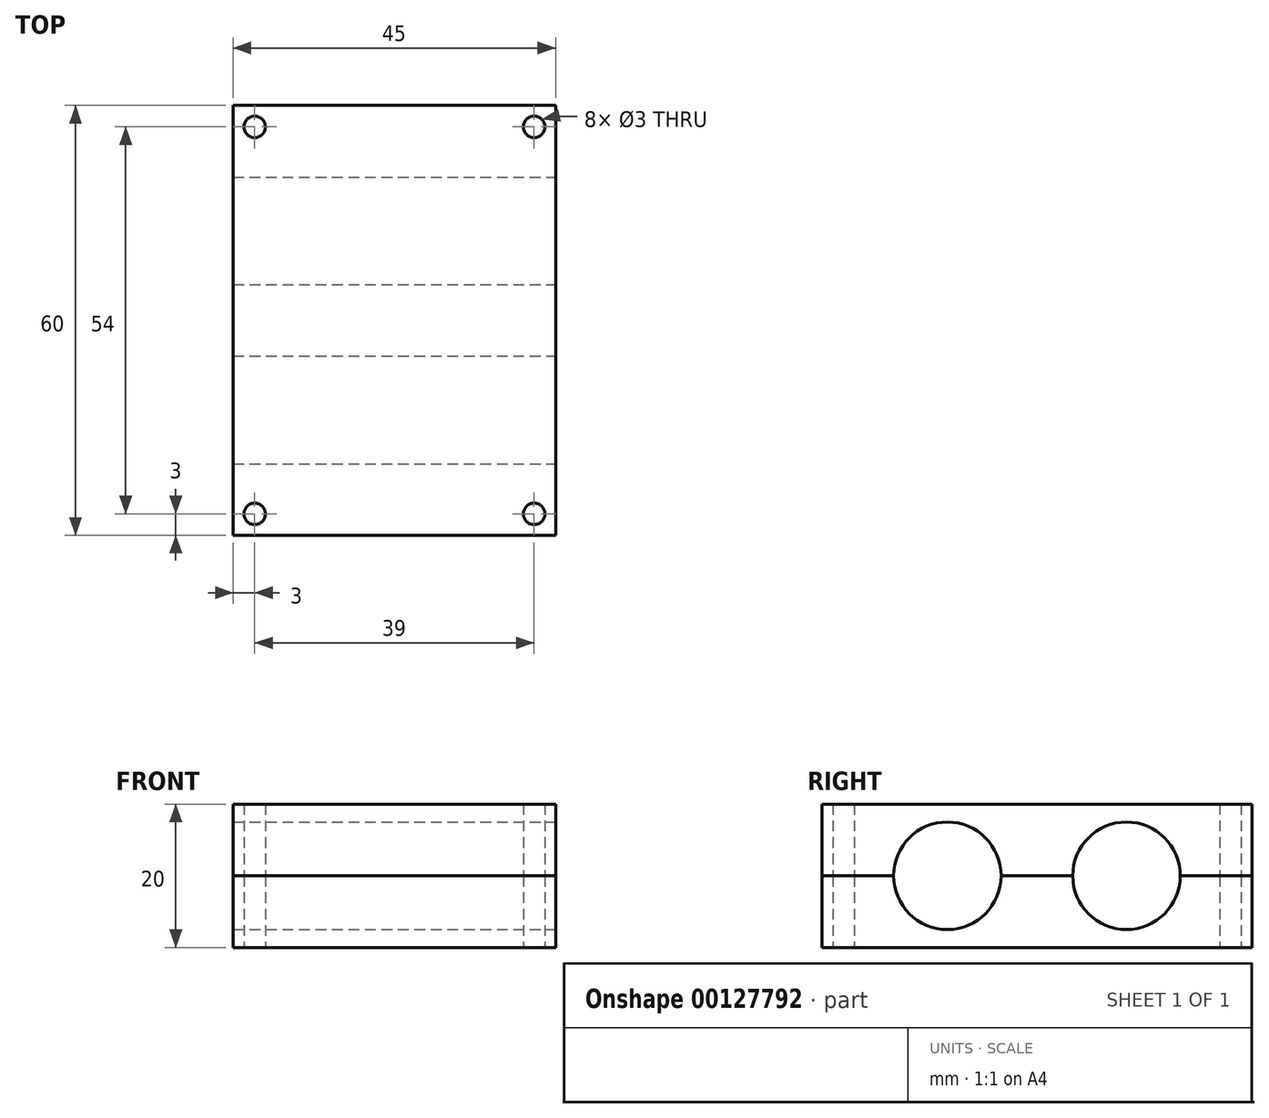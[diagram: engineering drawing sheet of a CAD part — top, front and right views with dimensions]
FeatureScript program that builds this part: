
annotation { "Feature Type Name" : "Feature", "Feature Type Description" : "" }
export const myFeature = defineFeature(function(context is Context, id is Id, definition is map)
    precondition{}
    {
        {
            var Q0;
            Q0=qCreatedBy(makeId("Right.planeOp"),FACE);
            var sketch = newSketch(context, id + "F0", { "sketchPlane" : qUnion([Q0])});
            skLineSegment(sketch, "E0", {"start": v(30, 0) * mm, "end": v(-30, 0) * mm});
            skLineSegment(sketch, "E1", {"start": v(-30, 0) * mm, "end": v(-30, 10) * mm});
            skLineSegment(sketch, "E2", {"start": v(0, 0) * mm, "end": v(0, -33.58) * mm, "construction": true});
            skLineSegment(sketch, "E3.MirrorCS", {"start": v(30, 0) * mm, "end": v(30, 10) * mm});
            skLineSegment(sketch, "E4.MirrorCS", {"start": v(30, 10) * mm, "end": v(-30, 10) * mm});
            skSolve(sketch);
        }
        {
            var Q0;
            Q0 = qSketchRegion(id + "F0", true);
            extrude(context, id + "F1", {"entities" : qUnion([Q0]), "endBound" : BoundingType.SYMMETRIC, "depth" : 45 * mm});
        }
        {
            var Q0;
            Q0=makeQuery(id+"F1.opExtrude","SWEPT_FACE",FACE,{"disambiguationData":[OSD([sQuery(id+"F0.wireOp",EDGE,"E0")])]});
            extrude(context, id + "F2", {"entities" : qUnion([Q0]), "depth" : 10 * mm});
        }
        {
            var Q0;
            Q0=makeQuery(id+"F1.opExtrude","CAP_FACE",FACE,{"disambiguationData":[OSD([sQuery(id+"F0.wireOp",EDGE,"E0"),sQuery(id+"F0.wireOp",EDGE,"E1"),sQuery(id+"F0.wireOp",EDGE,"128Ns7S3-iJ1R-hD63-Des7-Cw0FQeiLVcyu"),sQuery(id+"F0.wireOp",EDGE,"o8RlvnOk-mUnY-sZV7-Nvvh-wG9zo2OJw8qh"),sQuery(id+"F0.wireOp",EDGE,"HRAPB6wn-nVdK-lxr8-JZlT-5lnG8vlRGJTT"),sQuery(id+"F0.wireOp",EDGE,"45f2c6da-1243-415b-b326-b4a96a1e2a690.MirrorCS"),sQuery(id+"F0.wireOp",EDGE,"E3.MirrorCS"),sQuery(id+"F0.wireOp",EDGE,"E4.MirrorCS"),sQuery(id+"F0.wireOp",EDGE,"54c41837-7ab6-4fc5-a0fb-2d965c1fca7a0.MirrorCS"),sQuery(id+"F0.wireOp",EDGE,"8871dbe9-c1a3-435a-abf9-9d9c7d9c37b50.MirrorCS")])],"isStart":false});
            var sketch = newSketch(context, id + "F3", { "sketchPlane" : qUnion([Q0])});
            skCircle(sketch, "E5", {"center": v(-12.5, 0) * mm, "radius": 7.5 * mm});
            skCircle(sketch, "E6", {"center": v(12.5, 0) * mm, "radius": 7.5 * mm});
            skLineSegment(sketch, "E7", {"start": v(0, 0) * mm, "end": v(0, 23.63) * mm, "construction": true});
            skSolve(sketch);
        }
        {
            var Q0;
            Q0 = qSketchRegion(id + "F3", true);
            extrude(context, id + "F4", {"entities" : qUnion([Q0]), "operationType" : NewBodyOperationType.REMOVE, "endBound" : BoundingType.THROUGH_ALL, "oppositeDirection" : true, "depth" : 25 * mm});
        }
        {
            var Q0;
            Q0=makeQuery(id+"F2.opExtrude","CAP_FACE",FACE,{"disambiguationData":[OSD([sQuery(id+"F0.wireOp",EDGE,"E0")])],"isStart":false});
            var sketch = newSketch(context, id + "F5", { "sketchPlane" : qUnion([Q0])});
            skCircle(sketch, "E8", {"center": v(19.5, 27) * mm, "radius": 1.5 * mm});
            skLineSegment(sketch, "E9", {"start": v(0, 14.21) * mm, "end": v(0, 0) * mm, "construction": true});
            skLineSegment(sketch, "E10", {"start": v(0, 0) * mm, "end": v(13.91, 0) * mm, "construction": true});
            skCircle(sketch, "E11.MirrorC", {"center": v(-19.5, 27) * mm, "radius": 1.5 * mm});
            skCircle(sketch, "E12.MirrorC", {"center": v(19.5, -27) * mm, "radius": 1.5 * mm});
            skCircle(sketch, "E13.MirrorC", {"center": v(-19.5, -27) * mm, "radius": 1.5 * mm});
            skSolve(sketch);
        }
        {
            var Q0;
            Q0 = qSketchRegion(id + "F5", true);
            extrude(context, id + "F6", {"entities" : qUnion([Q0]), "operationType" : NewBodyOperationType.REMOVE, "endBound" : BoundingType.THROUGH_ALL, "oppositeDirection" : true, "depth" : 25 * mm});
        }
    });
